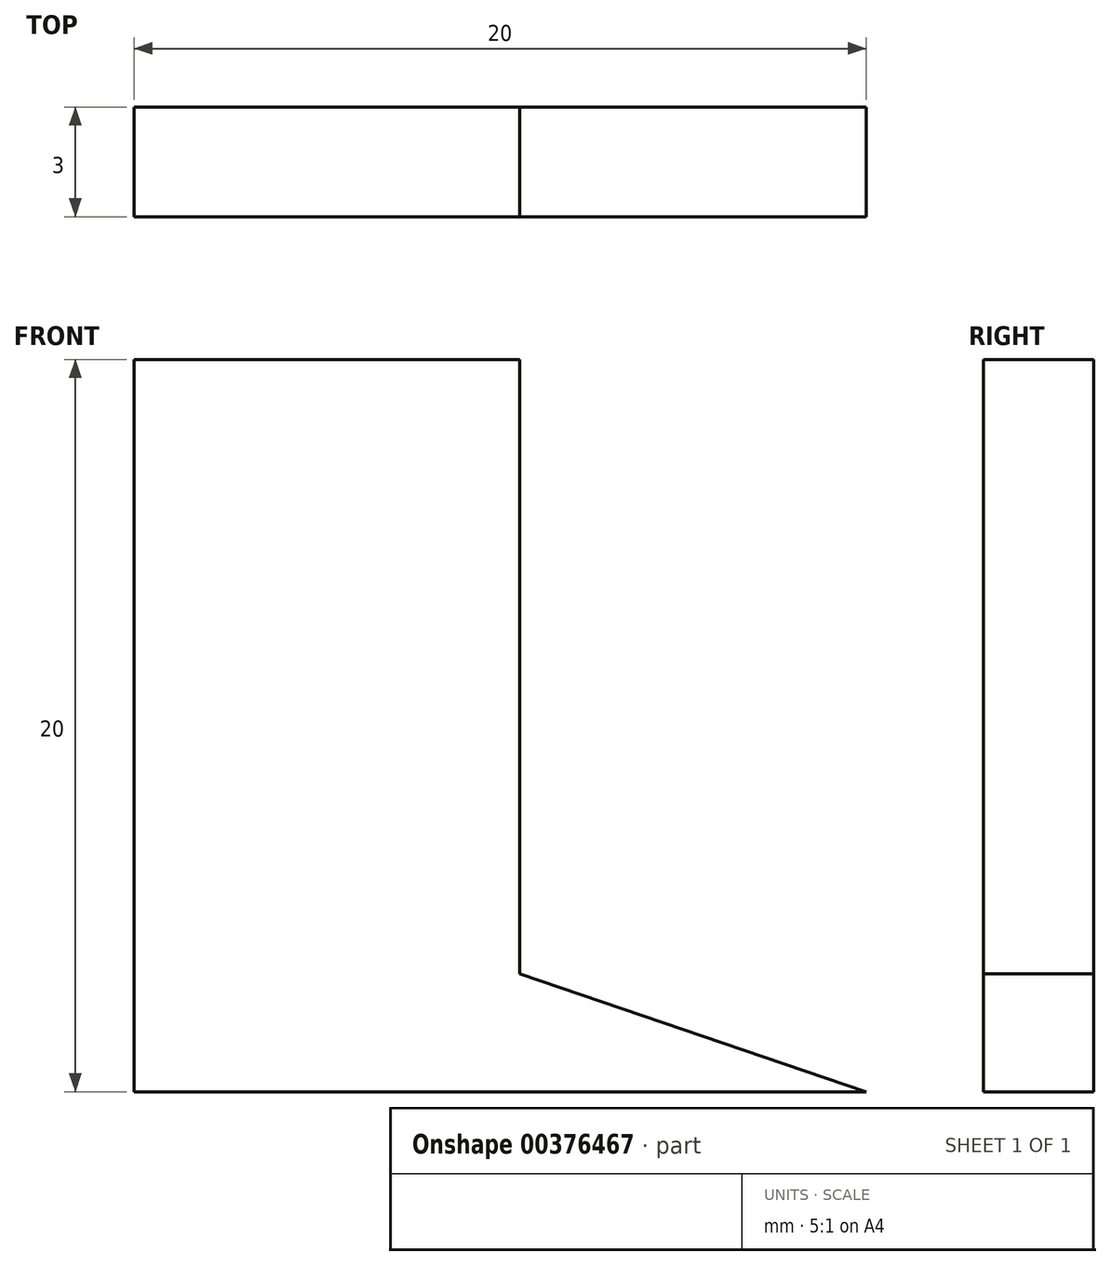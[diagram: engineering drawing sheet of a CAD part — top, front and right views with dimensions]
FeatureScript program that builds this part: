
annotation { "Feature Type Name" : "Feature", "Feature Type Description" : "" }
export const myFeature = defineFeature(function(context is Context, id is Id, definition is map)
    precondition{}
    {
        {
            var Q0;
            Q0=qCreatedBy(makeId("Front.planeOp"),FACE);
            var sketch = newSketch(context, id + "F0", { "sketchPlane" : qUnion([Q0])});
            skLineSegment(sketch, "E0", {"start": v(0, 0) * mm, "end": v(0, 20) * mm});
            skLineSegment(sketch, "E1", {"start": v(0, 0) * mm, "end": v(20, 0) * mm});
            skLineSegment(sketch, "E2", {"start": v(20, 0) * mm, "end": v(10.53, 3.22) * mm});
            skLineSegment(sketch, "E3", {"start": v(10.53, 3.22) * mm, "end": v(10.53, 20) * mm});
            skLineSegment(sketch, "E4", {"start": v(0, 20) * mm, "end": v(10.53, 20) * mm});
            skSolve(sketch);
        }
        {
            var Q0;
            Q0 = qSketchRegion(id + "F0", true);
            extrude(context, id + "F1", {"entities" : qUnion([Q0]), "depth" : 3 * mm});
        }
    });
